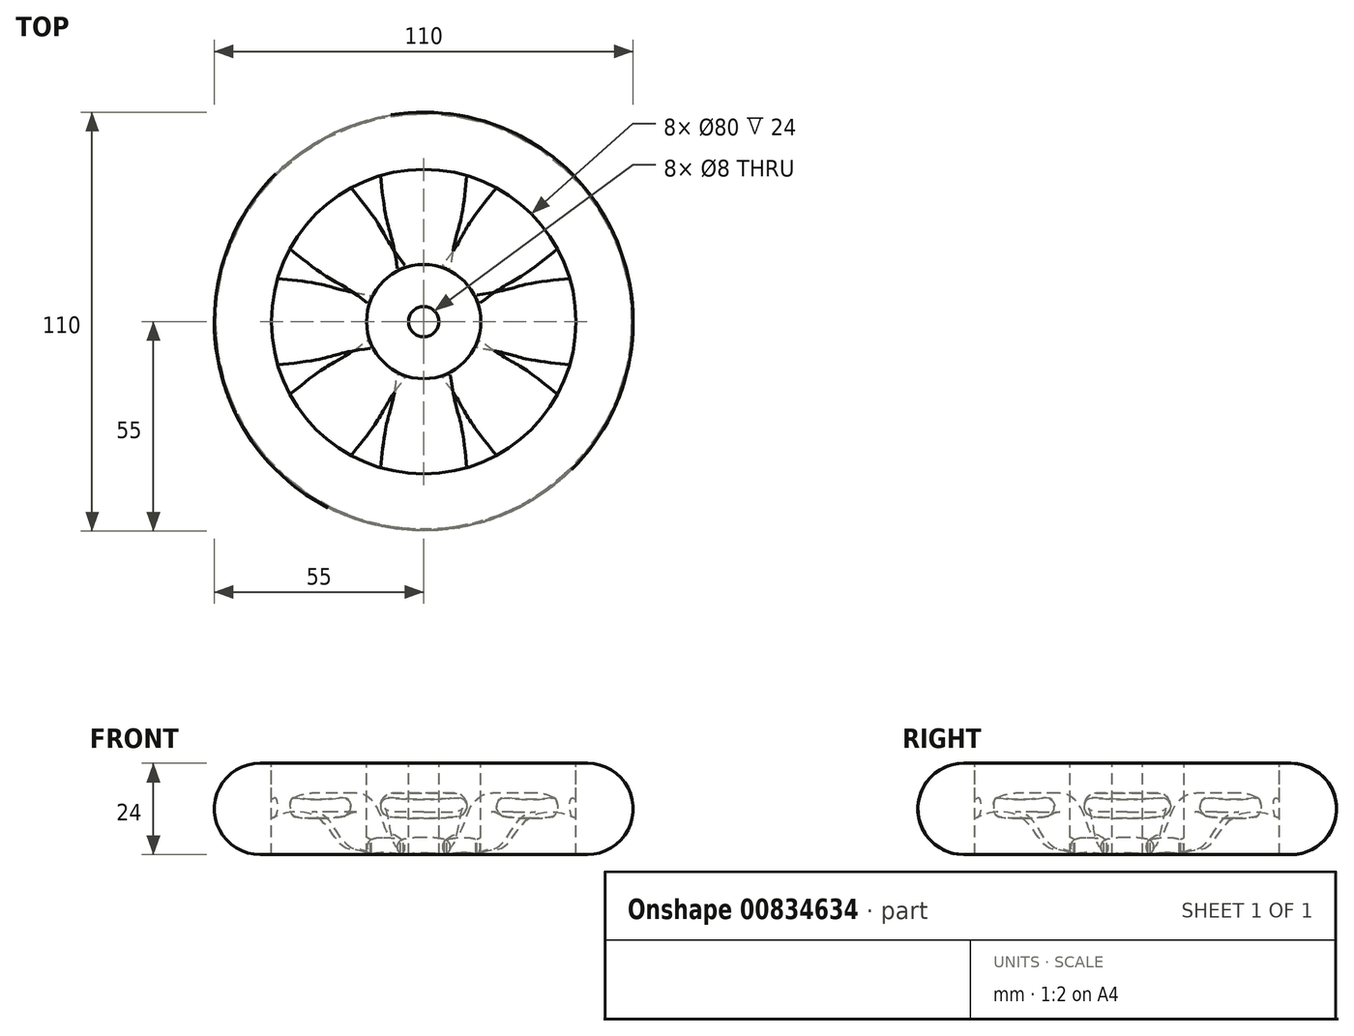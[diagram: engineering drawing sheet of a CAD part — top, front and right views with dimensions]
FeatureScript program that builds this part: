
annotation { "Feature Type Name" : "Feature", "Feature Type Description" : "" }
export const myFeature = defineFeature(function(context is Context, id is Id, definition is map)
    precondition{}
    {
        {
            var Q0;
            Q0=qCreatedBy(makeId("Top.planeOp"),FACE);
            var sketch = newSketch(context, id + "F0", { "sketchPlane" : qUnion([Q0])});
            skCircle(sketch, "E0", {"center": v(0, 0) * mm, "radius": 40 * mm});
            skSolve(sketch);
        }
        {
            var Q0;
            Q0=qCreatedBy(makeId("Front.planeOp"),FACE);
            var sketch = newSketch(context, id + "F1", { "sketchPlane" : qUnion([Q0])});
            skArc(sketch, "E1", {"start": v(-43, 12) * mm, "mid": v(-55, 0) * mm, "end": v(-43, -12) * mm});
            skLineSegment(sketch, "E2", {"start": v(-43, 12) * mm, "end": v(-40, 12) * mm});
            skLineSegment(sketch, "E3", {"start": v(-43, -12) * mm, "end": v(-40, -12) * mm});
            skLineSegment(sketch, "E4", {"start": v(-40, 12) * mm, "end": v(-40, -12) * mm});
            skSolve(sketch);
        }
        {
            var Q0;
            Q0 = qSketchRegion(id + "F1", true);
            var Q1;
            Q1 = qConstructionFilter(qBodyType(qCreatedBy(id + "F0" ,EDGE), BodyType.WIRE), ConstructionObject.NO);
            sweep(context, id + "F2", {"profiles" : qUnion([Q0]), "path" : qUnion([Q1])});
        }
        {
            var Q0;
            Q0=qCreatedBy(makeId("Right.planeOp"),FACE);
            cPlane(context, id + "F3", {"entities" : qUnion([Q0]), "cplaneType" : CPlaneType.OFFSET, "offset" : 40 * mm, "width" : 150 * mm, "height" : 150 * mm});
        }
        {
            var Q0;
            Q0=qCreatedBy(id+"F3.planeOp",FACE);
            var sketch = newSketch(context, id + "F4", { "sketchPlane" : qUnion([Q0])});
            skLineSegment(sketch, "E5", {"start": v(-9, 0) * mm, "end": v(9, 0) * mm});
            skArc(sketch, "E6.0.startCap", {"start": v(-9, -2.5) * mm, "mid": v(-11.5, 0) * mm, "end": v(-9, 2.5) * mm});
            skArc(sketch, "E6.0.endCap", {"start": v(9, 2.5) * mm, "mid": v(11.5, 0) * mm, "end": v(9, -2.5) * mm});
            skLineSegment(sketch, "E6.0.left", {"start": v(-9, 2.5) * mm, "end": v(9, 2.5) * mm});
            skLineSegment(sketch, "E6.0.right", {"start": v(-9, -2.5) * mm, "end": v(9, -2.5) * mm});
            skSolve(sketch);
        }
        {
            var Q0;
            Q0=qCreatedBy(makeId("Right.planeOp"),FACE);
            cPlane(context, id + "F5", {"entities" : qUnion([Q0]), "cplaneType" : CPlaneType.OFFSET, "offset" : 14 * mm, "width" : 150 * mm, "height" : 150 * mm});
        }
        {
            var Q0;
            Q0=qCreatedBy(id+"F5.planeOp",FACE);
            var sketch = newSketch(context, id + "F6", { "sketchPlane" : qUnion([Q0])});
            skLineSegment(sketch, "E7", {"start": v(-5, -10) * mm, "end": v(5, -10) * mm});
            skArc(sketch, "E8.0.startCap", {"start": v(-5, -12) * mm, "mid": v(-7, -10) * mm, "end": v(-5, -8) * mm});
            skArc(sketch, "E8.0.endCap", {"start": v(5, -8) * mm, "mid": v(7, -10) * mm, "end": v(5, -12) * mm});
            skLineSegment(sketch, "E8.0.left", {"start": v(-5, -8) * mm, "end": v(5, -8) * mm});
            skLineSegment(sketch, "E8.0.right", {"start": v(-5, -12) * mm, "end": v(5, -12) * mm});
            skSolve(sketch);
        }
        {
            var Q0;
            Q0=qCreatedBy(makeId("Front.planeOp"),FACE);
            var sketch = newSketch(context, id + "F7", { "sketchPlane" : qUnion([Q0])});
            skFitSpline(sketch, "E9", {"points": [v(14, -12) * mm, v(20.44, -10.27) * mm, v(24.06, -6.43) * mm, v(28.41, -1.97) * mm, v(40, -2.5) * mm], "startDerivative": vector(37.83, 21.17) * mm, "endDerivative": vector(47.32, -23.74) * mm});
            skSolve(sketch);
        }
        {
            var Q1;
            Q1 = qSketchRegion(id + "F6", true);
            var Q2;
            Q2 = qSketchRegion(id + "F4", true);
            var Q3;
            Q3 = qConstructionFilter(qBodyType(qCreatedBy(id + "F7" ,EDGE), BodyType.WIRE), ConstructionObject.NO);
            loft(context, id + "F8", {"operationType" : NewBodyOperationType.ADD, "addGuides" : true, "sheetProfilesArray" : [{ "sheetProfileEntities" : qUnion([Q1]) }, { "sheetProfileEntities" : qUnion([Q2]) }], "guidesArray" : [{ "guideEntities" : qUnion([Q3]), "guideDerivativeType" : LoftGuideDerivativeType.DEFAULT, "guideDerivativeMagnitude" : 1 }]});
        }
        {
            var Q0;
            Q0=qCreatedBy(makeId("Front.planeOp"),FACE);
            var sketch = newSketch(context, id + "F9", { "sketchPlane" : qUnion([Q0])});
            skLineSegment(sketch, "E10.bottom", {"start": v(0, 12) * mm, "end": v(15, 12) * mm});
            skLineSegment(sketch, "E10.top", {"start": v(0, -12) * mm, "end": v(15, -12) * mm});
            skLineSegment(sketch, "E10.left", {"start": v(0, 12) * mm, "end": v(0, -12) * mm});
            skLineSegment(sketch, "E10.right", {"start": v(15, 12) * mm, "end": v(15, -12) * mm});
            skSolve(sketch);
        }
        {
            var Q0;
            Q0 = qSketchRegion(id + "F9", true);
            var Q1;
            Q1=sQuery(id+"F9.wireOp",EDGE,"E10.left");
            revolve(context, id + "F10", {"operationType" : NewBodyOperationType.ADD, "surfaceOperationType" : NewSurfaceOperationType.NEW, "entities" : qUnion([Q0]), "axis" : qUnion([Q1]), "revolveType" : RevolveType.FULL});
        }
        {
            var Q0;
            Q0=makeQuery(id+"F2.opSweep","SWEPT_BODY",BODY,{"disambiguationData":[OSD([sQuery(id+"F0.wireOp",EDGE,"E0"),sQuery(id+"F1.wireOp",EDGE,"E1"),sQuery(id+"F1.wireOp",EDGE,"E2"),sQuery(id+"F1.wireOp",EDGE,"E3"),sQuery(id+"F1.wireOp",EDGE,"E4")])]});
            var Q1;
            Q1=makeQuery(id+"F2.opSweep","SWEPT_FACE",FACE,{"disambiguationData":[OSD([sQuery(id+"F0.wireOp",EDGE,"E0"),sQuery(id+"F1.wireOp",EDGE,"E4")])]});
            circularPattern(context, id + "F11", {"entities" : qUnion([Q0]), "axis" : qUnion([Q1]), "angle" : 360 * degree, "instanceCount" : 8, "oppositeDirection" : true, "equalSpace" : true});
        }
        {
            var Q0;
            Q0=makeQuery(id+"F10.opRevolve","SWEPT_FACE",FACE,{"disambiguationData":[OSD([sQuery(id+"F9.wireOp",EDGE,"E10.bottom")])]});
            var sketch = newSketch(context, id + "F12", { "sketchPlane" : qUnion([Q0])});
            skPoint(sketch, "E11", {"position": v(0, 0) * mm});
            skSolve(sketch);
        }
        {
            var Q0;
            Q0=sQuery(id+"F12.wireOp",VERTEX,"E11");
            var Q1;
            Q1=makeQuery(id+"F2.opSweep","SWEPT_BODY",BODY,{"disambiguationData":[OSD([sQuery(id+"F0.wireOp",EDGE,"E0"),sQuery(id+"F1.wireOp",EDGE,"E1"),sQuery(id+"F1.wireOp",EDGE,"E2"),sQuery(id+"F1.wireOp",EDGE,"E3"),sQuery(id+"F1.wireOp",EDGE,"E4")])]});
            var Q2;
            Q2=makeQuery(id+"F11.opPattern","COPY",BODY,{"derivedFrom":makeQuery(id+"F2.opSweep","SWEPT_BODY",BODY,{"disambiguationData":[OSD([sQuery(id+"F0.wireOp",EDGE,"E0"),sQuery(id+"F1.wireOp",EDGE,"E1"),sQuery(id+"F1.wireOp",EDGE,"E2"),sQuery(id+"F1.wireOp",EDGE,"E3"),sQuery(id+"F1.wireOp",EDGE,"E4")])]}),"instanceName":"1"});
            var Q3;
            Q3=makeQuery(id+"F11.opPattern","COPY",BODY,{"derivedFrom":makeQuery(id+"F2.opSweep","SWEPT_BODY",BODY,{"disambiguationData":[OSD([sQuery(id+"F0.wireOp",EDGE,"E0"),sQuery(id+"F1.wireOp",EDGE,"E1"),sQuery(id+"F1.wireOp",EDGE,"E2"),sQuery(id+"F1.wireOp",EDGE,"E3"),sQuery(id+"F1.wireOp",EDGE,"E4")])]}),"instanceName":"2"});
            var Q4;
            Q4=makeQuery(id+"F11.opPattern","COPY",BODY,{"derivedFrom":makeQuery(id+"F2.opSweep","SWEPT_BODY",BODY,{"disambiguationData":[OSD([sQuery(id+"F0.wireOp",EDGE,"E0"),sQuery(id+"F1.wireOp",EDGE,"E1"),sQuery(id+"F1.wireOp",EDGE,"E2"),sQuery(id+"F1.wireOp",EDGE,"E3"),sQuery(id+"F1.wireOp",EDGE,"E4")])]}),"instanceName":"3"});
            var Q5;
            Q5=makeQuery(id+"F11.opPattern","COPY",BODY,{"derivedFrom":makeQuery(id+"F2.opSweep","SWEPT_BODY",BODY,{"disambiguationData":[OSD([sQuery(id+"F0.wireOp",EDGE,"E0"),sQuery(id+"F1.wireOp",EDGE,"E1"),sQuery(id+"F1.wireOp",EDGE,"E2"),sQuery(id+"F1.wireOp",EDGE,"E3"),sQuery(id+"F1.wireOp",EDGE,"E4")])]}),"instanceName":"4"});
            var Q6;
            Q6=makeQuery(id+"F11.opPattern","COPY",BODY,{"derivedFrom":makeQuery(id+"F2.opSweep","SWEPT_BODY",BODY,{"disambiguationData":[OSD([sQuery(id+"F0.wireOp",EDGE,"E0"),sQuery(id+"F1.wireOp",EDGE,"E1"),sQuery(id+"F1.wireOp",EDGE,"E2"),sQuery(id+"F1.wireOp",EDGE,"E3"),sQuery(id+"F1.wireOp",EDGE,"E4")])]}),"instanceName":"5"});
            var Q7;
            Q7=makeQuery(id+"F11.opPattern","COPY",BODY,{"derivedFrom":makeQuery(id+"F2.opSweep","SWEPT_BODY",BODY,{"disambiguationData":[OSD([sQuery(id+"F0.wireOp",EDGE,"E0"),sQuery(id+"F1.wireOp",EDGE,"E1"),sQuery(id+"F1.wireOp",EDGE,"E2"),sQuery(id+"F1.wireOp",EDGE,"E3"),sQuery(id+"F1.wireOp",EDGE,"E4")])]}),"instanceName":"6"});
            var Q8;
            Q8=makeQuery(id+"F11.opPattern","COPY",BODY,{"derivedFrom":makeQuery(id+"F2.opSweep","SWEPT_BODY",BODY,{"disambiguationData":[OSD([sQuery(id+"F0.wireOp",EDGE,"E0"),sQuery(id+"F1.wireOp",EDGE,"E1"),sQuery(id+"F1.wireOp",EDGE,"E2"),sQuery(id+"F1.wireOp",EDGE,"E3"),sQuery(id+"F1.wireOp",EDGE,"E4")])]}),"instanceName":"7"});
            hole(context, id + "F13", {"style" : HoleStyle.SIMPLE, "endStyle" : HoleEndStyle.THROUGH, "holeDiameter" : 8 * mm, "majorDiameter" : 5 * mm, "isTappedThrough" : true, "tappedDepth" : 12 * mm, "tapClearance" : 3, "locations" : qUnion([Q0]), "scope" : qUnion([Q1, Q2, Q3, Q4, Q5, Q6, Q7, Q8])});
        }
    });
